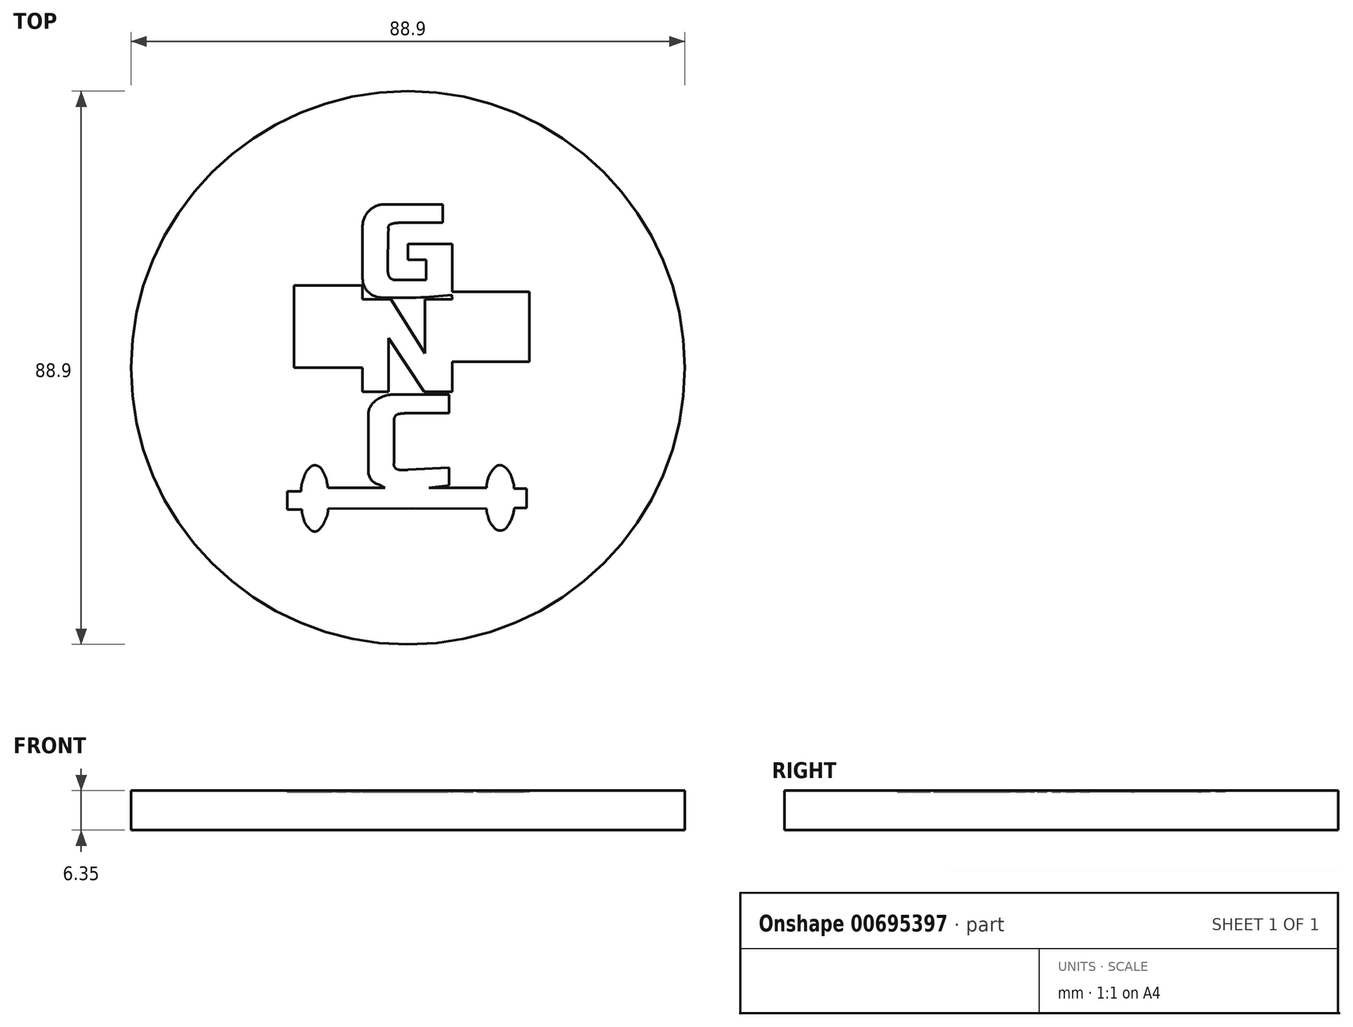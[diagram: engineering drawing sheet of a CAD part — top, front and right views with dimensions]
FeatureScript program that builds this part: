
annotation { "Feature Type Name" : "Feature", "Feature Type Description" : "" }
export const myFeature = defineFeature(function(context is Context, id is Id, definition is map)
    precondition{}
    {
        {
            var Q0;
            Q0=qCreatedBy(makeId("Top.planeOp"),FACE);
            var sketch = newSketch(context, id + "F0", { "sketchPlane" : qUnion([Q0])});
            skCircle(sketch, "E0", {"center": v(0, 0) * mm, "radius": 44.45 * mm});
            skSolve(sketch);
        }
        {
            var Q0;
            Q0=makeQuery(id+"F0.imprint","IMPRINT",FACE,{"disambiguationData":[TD([[makeQuery(id+"F0.imprint","IMPRINT",EDGE,{"derivedFrom":sQuery(id+"F0.wireOp",EDGE,"E0")}),1.0]])]});
            extrude(context, id + "F1", {"entities" : qUnion([Q0]), "depth" : 6.35 * mm, "offsetDistance" : 25.4 * mm});
        }
        {
            var Q0;
            Q0=makeQuery(id+"F1.opExtrude","CAP_FACE",FACE,{"disambiguationData":[OSD([sQuery(id+"F0.wireOp",EDGE,"E0")])],"isStart":false});
            var sketch = newSketch(context, id + "F2", { "sketchPlane" : qUnion([Q0])});
            skLineSegment(sketch, "E1", {"start": v(5.6, 26.26) * mm, "end": v(5.6, 23.3) * mm});
            skLineSegment(sketch, "E2", {"start": v(5.6, 23.3) * mm, "end": v(-1.47, 23.3) * mm});
            skLineSegment(sketch, "E3", {"start": v(-7.28, 22.7) * mm, "end": v(-7.28, 14.32) * mm});
            skLineSegment(sketch, "E4", {"start": v(-7.28, 13.2) * mm, "end": v(-18.3, 13.2) * mm});
            skLineSegment(sketch, "E5", {"start": v(-18.3, 13.2) * mm, "end": v(-18.3, 0) * mm});
            skLineSegment(sketch, "E6", {"start": v(-18.3, 0) * mm, "end": v(-7.28, 0) * mm});
            skLineSegment(sketch, "E7", {"start": v(-7.28, 0) * mm, "end": v(-7.28, -3.85) * mm});
            skLineSegment(sketch, "E8", {"start": v(-7.28, -3.85) * mm, "end": v(-6.28, -3.85) * mm});
            skLineSegment(sketch, "E9", {"start": v(17.1, -22.5) * mm, "end": v(17.08, -22.5) * mm});
            skLineSegment(sketch, "E10", {"start": v(7.1, 19.86) * mm, "end": v(7.1, 12.21) * mm});
            skLineSegment(sketch, "E11", {"start": v(7.1, 12.21) * mm, "end": v(7.1, 19.86) * mm});
            skLineSegment(sketch, "E12", {"start": v(0, 19.86) * mm, "end": v(7.1, 19.86) * mm});
            skLineSegment(sketch, "E13", {"start": v(19.5, 12.21) * mm, "end": v(7.1, 12.21) * mm});
            skLineSegment(sketch, "E14", {"start": v(19.5, 12.21) * mm, "end": v(19.5, 0.97) * mm});
            skLineSegment(sketch, "E15", {"start": v(19.5, 0.97) * mm, "end": v(7.1, 0.97) * mm});
            skLineSegment(sketch, "E16", {"start": v(6.62, -7.3) * mm, "end": v(0, -7.3) * mm});
            skLineSegment(sketch, "E17", {"start": v(0, -95.13) * mm, "end": v(7.1, -95.13) * mm});
            skLineSegment(sketch, "E18", {"start": v(0, 17.36) * mm, "end": v(2.94, 17.36) * mm});
            skLineSegment(sketch, "E19", {"start": v(2.94, 17.36) * mm, "end": v(2.94, 14.13) * mm});
            skLineSegment(sketch, "E20", {"start": v(2.94, 14.13) * mm, "end": v(0, 14.13) * mm});
            skLineSegment(sketch, "E21", {"start": v(-3.14, 21.93) * mm, "end": v(-3.27, 16.12) * mm});
            skArc(sketch, "E22", {"start": v(-3.14, 21.93) * mm, "mid": v(-3.18, 21.58) * mm, "end": v(-3.16, 21.21) * mm});
            skLineSegment(sketch, "E23", {"start": v(-6.28, -3.85) * mm, "end": v(-3.14, -3.85) * mm});
            skLineSegment(sketch, "E24", {"start": v(-3.14, -3.85) * mm, "end": v(-3.14, 4.79) * mm});
            skLineSegment(sketch, "E25", {"start": v(-3.14, 4.79) * mm, "end": v(2.62, -3.85) * mm});
            skLineSegment(sketch, "E26", {"start": v(2.62, -3.85) * mm, "end": v(7.1, -3.85) * mm});
            skLineSegment(sketch, "E27", {"start": v(7.1, -3.85) * mm, "end": v(7.1, 11) * mm});
            skLineSegment(sketch, "E28", {"start": v(7.1, 11) * mm, "end": v(2.71, 11) * mm});
            skLineSegment(sketch, "E29", {"start": v(2.71, 11) * mm, "end": v(2.71, 2.3) * mm});
            skLineSegment(sketch, "E30", {"start": v(2.71, 2.3) * mm, "end": v(-2.74, 11) * mm});
            skLineSegment(sketch, "E31", {"start": v(-2.74, 11) * mm, "end": v(-7.3, 11) * mm});
            skLineSegment(sketch, "E32", {"start": v(-6.35, -16.61) * mm, "end": v(-6.35, -7.45) * mm});
            skArc(sketch, "E33", {"start": v(-7.28, 22.7) * mm, "mid": v(-6.17, 25.29) * mm, "end": v(-3.54, 26.26) * mm});
            skPoint(sketch, "E34", {"position": v(-3.54, 26.26) * mm});
            skLineSegment(sketch, "E35", {"start": v(-3.54, 26.26) * mm, "end": v(5.6, 26.26) * mm});
            skLineSegment(sketch, "E36", {"start": v(-2.23, 14.13) * mm, "end": v(0, 14.13) * mm});
            skPoint(sketch, "E37", {"position": v(-7.3, 11) * mm});
            skLineSegment(sketch, "E38", {"start": v(-7.3, 11) * mm, "end": v(-7.28, 0) * mm});
            skLineSegment(sketch, "E39", {"start": v(-7.28, 13.2) * mm, "end": v(-7.3, 11) * mm});
            skLineSegment(sketch, "E40", {"start": v(6.62, -7.3) * mm, "end": v(6.62, -4.29) * mm});
            skLineSegment(sketch, "E41", {"start": v(6.62, -4.29) * mm, "end": v(-2.25, -4.29) * mm});
            skArc(sketch, "E42", {"start": v(-2.25, -4.29) * mm, "mid": v(-4.06, -4.64) * mm, "end": v(-5.6, -5.66) * mm});
            skArc(sketch, "E43", {"start": v(-5.6, -5.66) * mm, "mid": v(-6.15, -6.48) * mm, "end": v(-6.35, -7.45) * mm});
            skArc(sketch, "E44", {"start": v(0, -7.3) * mm, "mid": v(-0.83, -7.34) * mm, "end": v(-1.65, -7.45) * mm});
            skLineSegment(sketch, "E45", {"start": v(6.6, -16.03) * mm, "end": v(0, -16.4) * mm});
            skArc(sketch, "E46", {"start": v(0, -16.4) * mm, "mid": v(-0.71, -16.41) * mm, "end": v(-1.43, -16.4) * mm});
            skArc(sketch, "E47", {"start": v(-1.43, -16.4) * mm, "mid": v(-2.08, -16.05) * mm, "end": v(-2.25, -15.34) * mm});
            skArc(sketch, "E48", {"start": v(-6.35, -16.61) * mm, "mid": v(-5.88, -18) * mm, "end": v(-4.65, -18.78) * mm});
            skLineSegment(sketch, "E49", {"start": v(6.6, -16.03) * mm, "end": v(6.63, -18.9) * mm});
            skLineSegment(sketch, "E50", {"start": v(-2.25, -15.34) * mm, "end": v(-2.25, -8.46) * mm});
            skArc(sketch, "E51", {"start": v(-2.25, -8.46) * mm, "mid": v(-2.09, -7.87) * mm, "end": v(-1.65, -7.45) * mm});
            skArc(sketch, "E52", {"start": v(-1.47, 23.3) * mm, "mid": v(-2.14, 23.23) * mm, "end": v(-2.8, 23.05) * mm});
            skLineSegment(sketch, "E53", {"start": v(0, 19.86) * mm, "end": v(0, 17.36) * mm});
            skArc(sketch, "E54", {"start": v(-3.27, 16.12) * mm, "mid": v(-3.24, 15.5) * mm, "end": v(-3.11, 14.9) * mm});
            skArc(sketch, "E55", {"start": v(-3.11, 14.9) * mm, "mid": v(-2.79, 14.38) * mm, "end": v(-2.23, 14.13) * mm});
            skArc(sketch, "E56", {"start": v(-3.14, 21.93) * mm, "mid": v(-3.12, 22.2) * mm, "end": v(-3.14, 22.46) * mm});
            skArc(sketch, "E57", {"start": v(-3.14, 22.46) * mm, "mid": v(-3.08, 22.82) * mm, "end": v(-2.8, 23.05) * mm});
            skArc(sketch, "E58", {"start": v(-7.28, 14.32) * mm, "mid": v(-6.46, 12.25) * mm, "end": v(-4.43, 11.32) * mm});
            skArc(sketch, "E59", {"start": v(-4.43, 11.32) * mm, "mid": v(1.3, 11.27) * mm, "end": v(7.03, 11.73) * mm});
            skLineSegment(sketch, "E60", {"start": v(7.1, 12.21) * mm, "end": v(7.03, 11.73) * mm});
            skLineSegment(sketch, "E61", {"start": v(7.03, 11.73) * mm, "end": v(7.1, 11) * mm});
            skLineSegment(sketch, "E62", {"start": v(6.63, -18.9) * mm, "end": v(3.39, -19.3) * mm});
            skLineSegment(sketch, "E63", {"start": v(-4.65, -18.78) * mm, "end": v(-3.7, -19.29) * mm});
            skLineSegment(sketch, "E64", {"start": v(12.5, -22.62) * mm, "end": v(12.51, -22.62) * mm});
            skLineSegment(sketch, "E65", {"start": v(-3.7, -19.29) * mm, "end": v(3.39, -19.3) * mm});
            skPoint(sketch, "E66.start.orphan", {"position": v(6.63, -19.32) * mm});
            skLineSegment(sketch, "E67", {"start": v(17.1, -22.5) * mm, "end": v(19.04, -22.5) * mm});
            skLineSegment(sketch, "E68", {"start": v(19.04, -22.5) * mm, "end": v(19.04, -19.44) * mm});
            skLineSegment(sketch, "E69", {"start": v(19.04, -19.44) * mm, "end": v(17.02, -19.41) * mm});
            skLineSegment(sketch, "E70", {"start": v(17.02, -19.41) * mm, "end": v(17.02, -19.04) * mm});
            skArc(sketch, "E71", {"start": v(17.02, -19.04) * mm, "mid": v(16.99, -18.73) * mm, "end": v(16.91, -18.44) * mm});
            skLineSegment(sketch, "E72", {"start": v(16.91, -18.44) * mm, "end": v(16.7, -17.68) * mm});
            skArc(sketch, "E73", {"start": v(16.7, -17.68) * mm, "mid": v(16.4, -17) * mm, "end": v(15.99, -16.4) * mm});
            skArc(sketch, "E74", {"start": v(15.99, -16.4) * mm, "mid": v(15.66, -16.06) * mm, "end": v(15.29, -15.78) * mm});
            skArc(sketch, "E75", {"start": v(15.29, -15.78) * mm, "mid": v(14.67, -15.64) * mm, "end": v(14.1, -15.91) * mm});
            skLineSegment(sketch, "E76", {"start": v(14.1, -15.91) * mm, "end": v(13.94, -16.07) * mm});
            skArc(sketch, "E77", {"start": v(13.94, -16.07) * mm, "mid": v(13.22, -16.99) * mm, "end": v(12.78, -18.07) * mm});
            skArc(sketch, "E78", {"start": v(12.78, -18.07) * mm, "mid": v(12.76, -18.12) * mm, "end": v(12.75, -18.18) * mm});
            skArc(sketch, "E79", {"start": v(12.75, -18.18) * mm, "mid": v(12.65, -18.71) * mm, "end": v(12.6, -19.25) * mm});
            skLineSegment(sketch, "E80", {"start": v(12.6, -19.25) * mm, "end": v(12.6, -19.31) * mm});
            skLineSegment(sketch, "E81", {"start": v(9, -19.31) * mm, "end": v(12.6, -19.31) * mm});
            skLineSegment(sketch, "E82", {"start": v(9, -19.31) * mm, "end": v(3.39, -19.3) * mm});
            skLineSegment(sketch, "E83", {"start": v(12.51, -22.62) * mm, "end": v(0.57, -22.6) * mm});
            skLineSegment(sketch, "E84", {"start": v(17.1, -22.5) * mm, "end": v(17.01, -23) * mm});
            skArc(sketch, "E85", {"start": v(17.01, -23) * mm, "mid": v(16.56, -24.47) * mm, "end": v(15.74, -25.78) * mm});
            skArc(sketch, "E86", {"start": v(15.74, -25.78) * mm, "mid": v(15.6, -25.92) * mm, "end": v(15.42, -26.02) * mm});
            skArc(sketch, "E87", {"start": v(15.42, -26.02) * mm, "mid": v(14.9, -26.15) * mm, "end": v(14.35, -26.07) * mm});
            skArc(sketch, "E88", {"start": v(14.35, -26.07) * mm, "mid": v(14, -25.88) * mm, "end": v(13.76, -25.57) * mm});
            skLineSegment(sketch, "E89", {"start": v(13.76, -25.57) * mm, "end": v(13.6, -25.4) * mm});
            skArc(sketch, "E90", {"start": v(13.6, -25.4) * mm, "mid": v(13.11, -24.7) * mm, "end": v(12.88, -23.88) * mm});
            skLineSegment(sketch, "E91", {"start": v(12.51, -22.62) * mm, "end": v(12.63, -22.62) * mm});
            skLineSegment(sketch, "E92", {"start": v(12.63, -22.62) * mm, "end": v(12.63, -22.84) * mm});
            skArc(sketch, "E93", {"start": v(12.63, -22.84) * mm, "mid": v(12.7, -23.38) * mm, "end": v(12.88, -23.88) * mm});
            skLineSegment(sketch, "E94", {"start": v(0.57, -22.6) * mm, "end": v(-12.84, -22.62) * mm});
            skLineSegment(sketch, "E95", {"start": v(-3.7, -19.29) * mm, "end": v(-12.66, -19.26) * mm});
            skLineSegment(sketch, "E96", {"start": v(-12.66, -19.26) * mm, "end": v(-12.84, -19.26) * mm});
            skLineSegment(sketch, "E97", {"start": v(-12.84, -22.62) * mm, "end": v(-12.84, -22.92) * mm});
            skArc(sketch, "E98", {"start": v(-12.84, -22.92) * mm, "mid": v(-12.9, -23.55) * mm, "end": v(-13.12, -24.13) * mm});
            skArc(sketch, "E99", {"start": v(-13.12, -24.13) * mm, "mid": v(-13.28, -24.45) * mm, "end": v(-13.42, -24.77) * mm});
            skArc(sketch, "E100", {"start": v(-13.42, -24.77) * mm, "mid": v(-13.78, -25.44) * mm, "end": v(-14.26, -26.02) * mm});
            skArc(sketch, "E101", {"start": v(-14.26, -26.02) * mm, "mid": v(-14.97, -26.31) * mm, "end": v(-15.67, -26) * mm});
            skArc(sketch, "E102", {"start": v(-15.67, -26) * mm, "mid": v(-15.93, -25.73) * mm, "end": v(-16.18, -25.46) * mm});
            skArc(sketch, "E103", {"start": v(-16.18, -25.46) * mm, "mid": v(-16.47, -25.03) * mm, "end": v(-16.67, -24.55) * mm});
            skArc(sketch, "E104", {"start": v(-16.67, -24.55) * mm, "mid": v(-16.73, -24.33) * mm, "end": v(-16.8, -24.11) * mm});
            skArc(sketch, "E105", {"start": v(-16.8, -24.11) * mm, "mid": v(-16.9, -23.68) * mm, "end": v(-17.02, -23.26) * mm});
            skLineSegment(sketch, "E106", {"start": v(-17.02, -23.26) * mm, "end": v(-17.02, -22.8) * mm});
            skLineSegment(sketch, "E107", {"start": v(-19.39, -22.8) * mm, "end": v(-17.02, -22.8) * mm});
            skLineSegment(sketch, "E108", {"start": v(-19.39, -22.8) * mm, "end": v(-19.39, -19.85) * mm});
            skLineSegment(sketch, "E109", {"start": v(-19.39, -19.85) * mm, "end": v(-17.14, -19.85) * mm});
            skLineSegment(sketch, "E110", {"start": v(-17.14, -19.85) * mm, "end": v(-17.14, -19.51) * mm});
            skArc(sketch, "E111", {"start": v(-17.14, -19.51) * mm, "mid": v(-17.1, -18.93) * mm, "end": v(-16.96, -18.36) * mm});
            skArc(sketch, "E112", {"start": v(-16.96, -18.36) * mm, "mid": v(-16.75, -17.73) * mm, "end": v(-16.52, -17.11) * mm});
            skArc(sketch, "E113", {"start": v(-16.52, -17.11) * mm, "mid": v(-16.15, -16.44) * mm, "end": v(-15.61, -15.9) * mm});
            skArc(sketch, "E114", {"start": v(-15.61, -15.9) * mm, "mid": v(-15.09, -15.67) * mm, "end": v(-14.52, -15.75) * mm});
            skArc(sketch, "E115", {"start": v(-14.52, -15.75) * mm, "mid": v(-14.05, -16.05) * mm, "end": v(-13.73, -16.5) * mm});
            skArc(sketch, "E116", {"start": v(-13.73, -16.5) * mm, "mid": v(-13.57, -16.84) * mm, "end": v(-13.4, -17.16) * mm});
            skArc(sketch, "E117", {"start": v(-13.4, -17.16) * mm, "mid": v(-13.1, -17.89) * mm, "end": v(-12.99, -18.66) * mm});
            skLineSegment(sketch, "E118", {"start": v(-12.84, -19.26) * mm, "end": v(-12.99, -18.66) * mm});
            skSolve(sketch);
        }
        {
            var Q0;
            Q0 = qSketchRegion(id + "F2", true);
            extrude(context, id + "F3", {"entities" : qUnion([Q0]), "operationType" : NewBodyOperationType.REMOVE, "oppositeDirection" : true, "depth" : 0.25 * mm, "offsetDistance" : 25.4 * mm});
        }
    });
